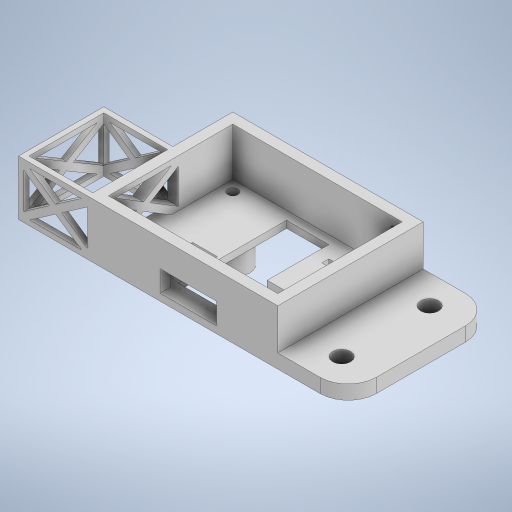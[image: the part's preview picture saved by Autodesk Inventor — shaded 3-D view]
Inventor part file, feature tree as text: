
AUTODESK INVENTOR PART (.ipt)
format: ipt  version: 2024 (Build 280153000, 153)  size: 582,656 bytes
history: native  units: in
note: dims shown in document units (in); Inventor stores cm internally (conversion verified against a paired STEP export)
features: extrude x15, sketch x15, fillet x1
ambient origin geometry x8: Origin, YZ Plane, XZ Plane, XY Plane, X Axis, Y Axis, Z Axis, Center Point
bodies: Solid1 (feature_tree)
feature tree (31):
  extrude  "Extrusion1"  Depth=1.725in
  extrude  "Extrusion2"  Depth=0.065in
  extrude  "Extrusion3"  Depth=0.135in
  extrude  "Extrusion4"  Depth=0.135in
  extrude  "Extrusion5"  Depth=0.145in
  fillet  "Fillet1"  Radius=0.145in
  extrude  "Extrusion6"  Depth=0.145in
  extrude  "Extrusion7"  Depth=0.15in
  extrude  "Extrusion8"  Depth=0.4in
  extrude  "Extrusion9"  Depth=0.1in
  extrude  "Extrusion10"  Depth=0.3in
  extrude  "Extrusion11"  Depth=0.325in
  extrude  "Extrusion12"  Depth=0.1in
  extrude  "Extrusion13"  Depth=0.1in
  extrude  "Extrusion14"  Depth=0.6in
  extrude  "Extrusion15"  Depth=0.35in
  sketch  "Sketch1"  dims[d0=2.365in d1=1.725in]
  sketch  "Sketch2"  dims[d2=0.02in d3=0.065in]
  sketch  "Sketch3"  dims[d4=0.135in d5=0.135in]
  sketch  "Sketch4"  dims[d6=0.135in d7=0.135in]
  sketch  "Sketch5"  dims[d8=0.135in d9=0.145in d10=0.145in]
  sketch  "Sketch6"  dims[d11=0.145in d12=0.145in]
  sketch  "Sketch7"  dims[d13=0.1in d14=0.0in d15=0.15in]
  sketch  "Sketch8"  dims[d16=0.78in d17=0.0in d18=0.4in]
  sketch  "Sketch9"  dims[d19=0.4in d20=0.1in]
  sketch  "Sketch10"  dims[d21=0.24in d22=0.3in]
  sketch  "Sketch11"  dims[d23=0.625in d24=0.325in]
  sketch  "Sketch12"  dims[d25=0.2in d26=0.1in]
  sketch  "Sketch13"  dims[d27=0.9in d28=0.1in]
  sketch  "Sketch14"  dims[d29=0.6in d30=0.85in]
  sketch  "Sketch15"  dims[d31=0.45in d32=0.35in d33=1.05in d34=0.4in d35=0.7in d36=0.08in d37=0.8in d38=0.15in d39=0.275in d40=0.15in d41=0.56in d42=0.47in d43=0.45in d44=0.35in d45=0.235in d46=0.87in d47=0.8in d48=0.3in d49=0.15in d50=0.0in d51=0.2in d52=1.0in d53=0.0in d54=1.0in d55=1.25in d56=0.255in d57=0.255in d58=1.0in d59=0.0in d60=0.4in d61=0.4in d62=0.37in d63=0.0in d64=0.37in d65=0.0in d66=0.17in d67=1.0in d68=0.0in d69=0.075in d70=0.9055in d71=1.063in d72=0.075in d73=1.0in d74=0.0in d75=0.075in d76=1.0in d77=0.0in d78=0.63in d79=0.05in d80=0.05in d81=0.05in d82=0.05in d83=2.0in d84=0.0in d85=1.063in d86=0.63in d87=0.05in d88=0.05in d89=0.05in d90=0.05in d91=0.1in d92=0.0in d93=0.075in d94=0.05in d95=0.05in d96=0.05in d97=0.05in d98=0.2in d99=0.0in d100=0.05in d101=0.05in d102=0.05in d103=0.05in d104=0.4in d105=0.2in d106=0.0in d107=1.0in d108=0.0in]
